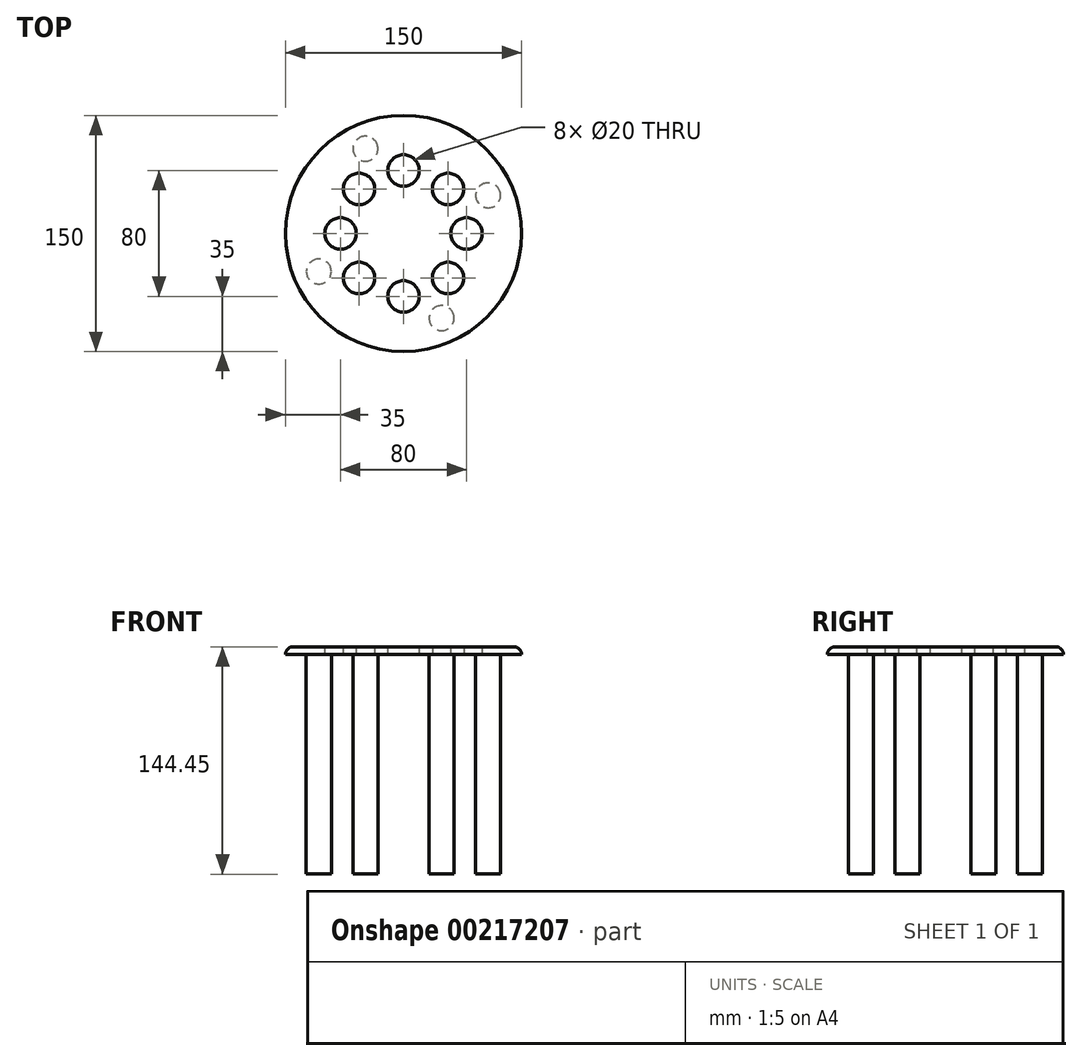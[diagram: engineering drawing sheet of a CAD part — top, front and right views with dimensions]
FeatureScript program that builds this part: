
annotation { "Feature Type Name" : "Feature", "Feature Type Description" : "" }
export const myFeature = defineFeature(function(context is Context, id is Id, definition is map)
    precondition{}
    {
        {
            var Q0;
            Q0=qCreatedBy(makeId("Top.planeOp"),FACE);
            var sketch = newSketch(context, id + "F0", { "sketchPlane" : qUnion([Q0])});
            skCircle(sketch, "E0", {"center": v(0, 0) * mm, "radius": 75 * mm});
            skCircle(sketch, "E1", {"center": v(0, 40) * mm, "radius": 10 * mm});
            skCircle(sketch, "E2.1.0", {"center": v(-28.28, 28.28) * mm, "radius": 10 * mm});
            skCircle(sketch, "E2.2.0", {"center": v(-40, 0) * mm, "radius": 10 * mm});
            skCircle(sketch, "E2.3.0", {"center": v(-28.28, -28.28) * mm, "radius": 10 * mm});
            skCircle(sketch, "E2.4.0", {"center": v(0, -40) * mm, "radius": 10 * mm});
            skCircle(sketch, "E2.5.0", {"center": v(28.28, -28.28) * mm, "radius": 10 * mm});
            skCircle(sketch, "E2.6.0", {"center": v(40, 0) * mm, "radius": 10 * mm});
            skCircle(sketch, "E2.7.0", {"center": v(28.28, 28.28) * mm, "radius": 10 * mm});
            skSolve(sketch);
        }
        {
            var Q0;
            Q0=makeQuery(id+"F0.imprint","IMPRINT",FACE,{"disambiguationData":[TD([[makeQuery(id+"F0.imprint","IMPRINT",EDGE,{"derivedFrom":sQuery(id+"F0.wireOp",EDGE,"E0")}),1.0]])]});
            extrude(context, id + "F1", {"entities" : qUnion([Q0]), "depth" : 5 * mm});
        }
        {
            var Q0;
            Q0=makeQuery(id+"F1.opExtrude","CAP_EDGE",EDGE,{"disambiguationData":[OSD([sQuery(id+"F0.wireOp",EDGE,"E0")])],"isStart":false});
            fillet(context, id + "F2", {"entities" : qUnion([Q0]), "radius" : 5.08 * mm, "tangentPropagation" : true, "allowEdgeOverflow" : false});
        }
        {
            var Q0;
            Q0=qCreatedBy(makeId("Top.planeOp"),FACE);
            var sketch = newSketch(context, id + "F3", { "sketchPlane" : qUnion([Q0])});
            skCircle(sketch, "E3", {"center": v(-24.2, 53.78) * mm, "radius": 7.96 * mm});
            skCircle(sketch, "E4.1.0", {"center": v(-53.78, -24.2) * mm, "radius": 7.96 * mm});
            skCircle(sketch, "E4.2.0", {"center": v(24.2, -53.78) * mm, "radius": 7.96 * mm});
            skCircle(sketch, "E4.3.0", {"center": v(53.78, 24.2) * mm, "radius": 7.96 * mm});
            skPoint(sketch, "E4.center", {"position": v(0, 0) * mm});
            skSolve(sketch);
        }
        {
            var Q0;
            Q0=makeQuery(id+"F3.imprint","IMPRINT",FACE,{"disambiguationData":[TD([[makeQuery(id+"F3.imprint","IMPRINT",EDGE,{"derivedFrom":sQuery(id+"F3.wireOp",EDGE,"E4.2.0")}),1.0]])]});
            var Q1;
            Q1=makeQuery(id+"F3.imprint","IMPRINT",FACE,{"disambiguationData":[TD([[makeQuery(id+"F3.imprint","IMPRINT",EDGE,{"derivedFrom":sQuery(id+"F3.wireOp",EDGE,"E4.3.0")}),1.0]])]});
            var Q2;
            Q2=makeQuery(id+"F3.imprint","IMPRINT",FACE,{"disambiguationData":[TD([[makeQuery(id+"F3.imprint","IMPRINT",EDGE,{"derivedFrom":sQuery(id+"F3.wireOp",EDGE,"E3")}),1.0]])]});
            var Q3;
            Q3=makeQuery(id+"F3.imprint","IMPRINT",FACE,{"disambiguationData":[TD([[makeQuery(id+"F3.imprint","IMPRINT",EDGE,{"derivedFrom":sQuery(id+"F3.wireOp",EDGE,"E4.1.0")}),1.0]])]});
            extrude(context, id + "F4", {"entities" : qUnion([Q0, Q1, Q2, Q3]), "operationType" : NewBodyOperationType.ADD, "oppositeDirection" : true, "depth" : 139.45 * mm});
        }
    });
